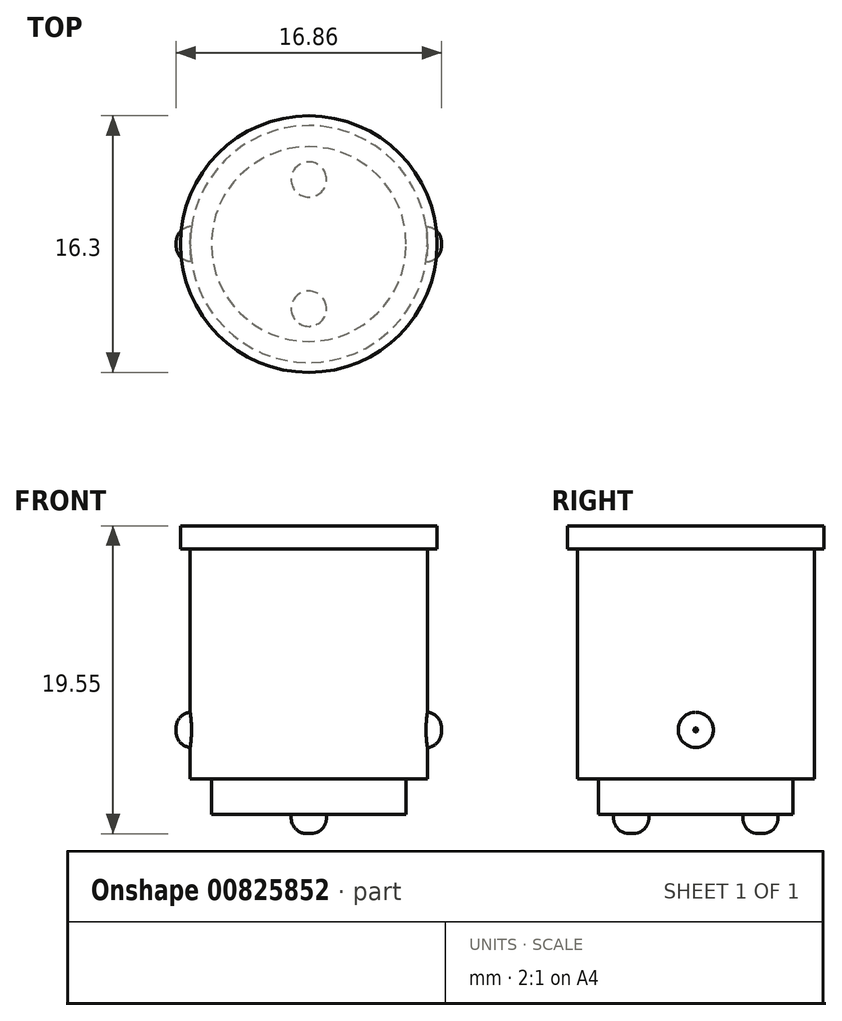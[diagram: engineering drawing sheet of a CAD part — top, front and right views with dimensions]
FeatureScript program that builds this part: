
annotation { "Feature Type Name" : "Feature", "Feature Type Description" : "" }
export const myFeature = defineFeature(function(context is Context, id is Id, definition is map)
    precondition{}
    {
        {
            var Q0;
            Q0=qCreatedBy(makeId("Front.planeOp"),FACE);
            var sketch = newSketch(context, id + "F0", { "sketchPlane" : qUnion([Q0])});
            skLineSegment(sketch, "E0.bottom", {"start": v(7.53, -8.03) * mm, "end": v(-7.53, -8.03) * mm});
            skLineSegment(sketch, "E0.top", {"start": v(7.53, 8.04) * mm, "end": v(-7.53, 8.04) * mm});
            skLineSegment(sketch, "E0.left", {"start": v(7.53, -8.03) * mm, "end": v(7.53, 8.04) * mm});
            skLineSegment(sketch, "E0.right", {"start": v(-7.53, -8.04) * mm, "end": v(-7.53, 8.04) * mm});
            skPoint(sketch, "E0.middle", {"position": v(0, 0) * mm});
            skLineSegment(sketch, "E1.bottom", {"start": v(6.19, -10.27) * mm, "end": v(-6.18, -10.27) * mm});
            skLineSegment(sketch, "E1.top", {"start": v(6.19, -5.8) * mm, "end": v(-6.18, -5.8) * mm});
            skLineSegment(sketch, "E1.left", {"start": v(6.19, -10.27) * mm, "end": v(6.19, -5.8) * mm});
            skLineSegment(sketch, "E1.right", {"start": v(-6.18, -10.27) * mm, "end": v(-6.18, -5.8) * mm});
            skPoint(sketch, "E1.middle", {"position": v(0, -8.03) * mm});
            skLineSegment(sketch, "E2.bottom", {"start": v(8.15, 6.57) * mm, "end": v(-8.15, 6.57) * mm});
            skLineSegment(sketch, "E2.top", {"start": v(8.15, 9.5) * mm, "end": v(-8.15, 9.5) * mm});
            skLineSegment(sketch, "E2.left", {"start": v(8.15, 6.57) * mm, "end": v(8.15, 9.5) * mm});
            skLineSegment(sketch, "E2.right", {"start": v(-8.15, 6.57) * mm, "end": v(-8.15, 9.5) * mm});
            skPoint(sketch, "E2.middle", {"position": v(0, 8.04) * mm});
            skLineSegment(sketch, "E3", {"start": v(-8.15, 8.04) * mm, "end": v(8.15, 8.04) * mm});
            skLineSegment(sketch, "E4", {"start": v(0, 9.5) * mm, "end": v(0, -10.27) * mm});
            skLineSegment(sketch, "E5", {"start": v(0, 8.04) * mm, "end": v(0, -6.03) * mm});
            skSolve(sketch);
        }
        {
            var Q0;
            {var subQ3=sQuery(id+"F0.wireOp",EDGE,"E0.bottom");var subQ7=sQuery(id+"F0.wireOp",EDGE,"E0.right");var subQ8=makeQuery(id+"F0.imprint","INTERSECT",VERTEX,{"derivedFrom":[subQ3,subQ7]});Q0=makeQuery(id+"F0.imprint","IMPRINT",FACE,{"disambiguationData":[TD([[makeQuery(id+"F0.imprint","IMPRINT",EDGE,{"disambiguationData":[TD([[subQ8,1.0]])],"derivedFrom":subQ3}),-1.0]])]});}
            var Q1;
            {var subQ0=sQuery(id+"F0.wireOp",EDGE,"E3");var subQ1=sQuery(id+"F0.wireOp",EDGE,"E0.right");var subQ2=makeQuery(id+"F0.imprint","INTERSECT",VERTEX,{"derivedFrom":[subQ1,subQ0]});Q1=makeQuery(id+"F0.imprint","IMPRINT",FACE,{"disambiguationData":[TD([[makeQuery(id+"F0.imprint","IMPRINT",EDGE,{"disambiguationData":[TD([[subQ2,1.0]])],"derivedFrom":subQ1}),-1.0]])]});}
            var Q2;
            {var subQ0=sQuery(id+"F0.wireOp",EDGE,"E3");var subQ1=sQuery(id+"F0.wireOp",EDGE,"E0.right");var subQ2=makeQuery(id+"F0.imprint","INTERSECT",VERTEX,{"derivedFrom":[subQ1,subQ0]});Q2=makeQuery(id+"F0.imprint","IMPRINT",FACE,{"disambiguationData":[TD([[makeQuery(id+"F0.imprint","IMPRINT",EDGE,{"disambiguationData":[TD([[subQ2,1.0]])],"derivedFrom":subQ1}),1.0]])]});}
            var Q3;
            {var subQ0=sQuery(id+"F0.wireOp",EDGE,"E1.right");var subQ1=sQuery(id+"F0.wireOp",EDGE,"E0.bottom");var subQ2=makeQuery(id+"F0.imprint","INTERSECT",VERTEX,{"derivedFrom":[subQ1,subQ0]});Q3=makeQuery(id+"F0.imprint","IMPRINT",FACE,{"disambiguationData":[TD([[makeQuery(id+"F0.imprint","IMPRINT",EDGE,{"disambiguationData":[TD([[subQ2,1.0]])],"derivedFrom":subQ1}),1.0]])]});}
            var Q4;
            {var subQ0=sQuery(id+"F0.wireOp",EDGE,"E1.right");var subQ1=sQuery(id+"F0.wireOp",EDGE,"E0.bottom");var subQ2=makeQuery(id+"F0.imprint","INTERSECT",VERTEX,{"derivedFrom":[subQ1,subQ0]});Q4=makeQuery(id+"F0.imprint","IMPRINT",FACE,{"disambiguationData":[TD([[makeQuery(id+"F0.imprint","IMPRINT",EDGE,{"disambiguationData":[TD([[subQ2,1.0]])],"derivedFrom":subQ1}),-1.0]])]});}
            var Q5;
            Q5=sQuery(id+"F0.wireOp",EDGE,"E4");
            revolve(context, id + "F1", {"surfaceOperationType" : NewSurfaceOperationType.NEW, "entities" : qUnion([Q0, Q1, Q2, Q3, Q4]), "axis" : qUnion([Q5]), "revolveType" : RevolveType.FULL});
        }
        {
            var Q0;
            Q0=qCreatedBy(makeId("Right.planeOp"),FACE);
            var sketch = newSketch(context, id + "F2", { "sketchPlane" : qUnion([Q0])});
            skLineSegment(sketch, "E6", {"start": v(0, 0) * mm, "end": v(0, -6.04) * mm});
            skCircle(sketch, "E7", {"center": v(0, -4.92) * mm, "radius": 1.12 * mm});
            skSolve(sketch);
        }
        {
            var Q0;
            Q0 = qSketchRegion(id + "F2", true);
            extrude(context, id + "F3", {"entities" : qUnion([Q0]), "operationType" : NewBodyOperationType.ADD, "oppositeDirection" : true, "depth" : 8.43 * mm, "offsetDistance" : 25 * mm, "hasSecondDirection" : true, "secondDirectionOppositeDirection" : false, "secondDirectionDepth" : 8.43 * mm});
        }
        {
            var Q0;
            Q0=makeQuery(id+"F3.opExtrude","CAP_FACE",FACE,{"disambiguationData":[OSD([sQuery(id+"F2.wireOp",EDGE,"E7")])],"isStart":false});
            var Q1;
            Q1=makeQuery(id+"F3.opExtrude","CAP_EDGE",EDGE,{"disambiguationData":[OSD([sQuery(id+"F2.wireOp",EDGE,"E7")])],"isStart":true});
            fillet(context, id + "F4", {"entities" : qUnion([Q0, Q1]), "radius" : 1 * mm, "tangentPropagation" : true, "allowEdgeOverflow" : false});
        }
        {
            var Q0;
            Q0=makeQuery(id+"F1.opRevolve","SWEPT_FACE",FACE,{"disambiguationData":[OSD([sQuery(id+"F0.wireOp",EDGE,"E1.bottom")])]});
            var sketch = newSketch(context, id + "F5", { "sketchPlane" : qUnion([Q0])});
            skSolve(sketch);
        }
        {
            var Q0;
            Q0=makeQuery(id+"F5.imprint","IMPRINT",FACE,{"disambiguationData":[TD([[makeQuery(id+"F5.imprint","IMPRINT",EDGE,{"derivedFrom":makeQuery(id+"F1.opRevolve","SWEPT_EDGE",EDGE,{"disambiguationData":[OSD([sQuery(id+"F0.wireOp",EDGE,"E1.bottom"),sQuery(id+"F0.wireOp",EDGE,"E1.right")])]})}),-1.0]])]});
            var sketch = newSketch(context, id + "F6", { "sketchPlane" : qUnion([Q0])});
            skCircle(sketch, "E8", {"center": v(0, 0) * mm, "radius": 6.18 * mm});
            skLineSegment(sketch, "E9", {"start": v(0, 6.18) * mm, "end": v(0, 5.22) * mm});
            skLineSegment(sketch, "E10", {"start": v(0, -6.18) * mm, "end": v(0, -5.22) * mm});
            skCircle(sketch, "E11", {"center": v(0, -4.1) * mm, "radius": 1.12 * mm});
            skCircle(sketch, "E12", {"center": v(0, 4.1) * mm, "radius": 1.12 * mm});
            skSolve(sketch);
        }
        {
            var Q0;
            Q0=makeQuery(id+"F6.imprint","IMPRINT",FACE,{"disambiguationData":[TD([[makeQuery(id+"F6.imprint","IMPRINT",EDGE,{"derivedFrom":sQuery(id+"F6.wireOp",EDGE,"E12")}),1.0]])]});
            var Q1;
            Q1=makeQuery(id+"F6.imprint","IMPRINT",FACE,{"disambiguationData":[TD([[makeQuery(id+"F6.imprint","IMPRINT",EDGE,{"derivedFrom":sQuery(id+"F6.wireOp",EDGE,"E11")}),1.0]])]});
            extrude(context, id + "F7", {"entities" : qUnion([Q0, Q1]), "operationType" : NewBodyOperationType.ADD, "depth" : 1.23 * mm, "offsetDistance" : 25 * mm});
        }
        {
            var Q0;
            Q0=makeQuery(id+"F7.opExtrude","CAP_EDGE",EDGE,{"disambiguationData":[OSD([sQuery(id+"F6.wireOp",EDGE,"E12")])],"isStart":false});
            var Q1;
            Q1=makeQuery(id+"F7.opExtrude","CAP_EDGE",EDGE,{"disambiguationData":[OSD([sQuery(id+"F6.wireOp",EDGE,"E11")])],"isStart":false});
            fillet(context, id + "F8", {"entities" : qUnion([Q0, Q1]), "radius" : 1 * mm, "tangentPropagation" : true, "allowEdgeOverflow" : false});
        }
    });
